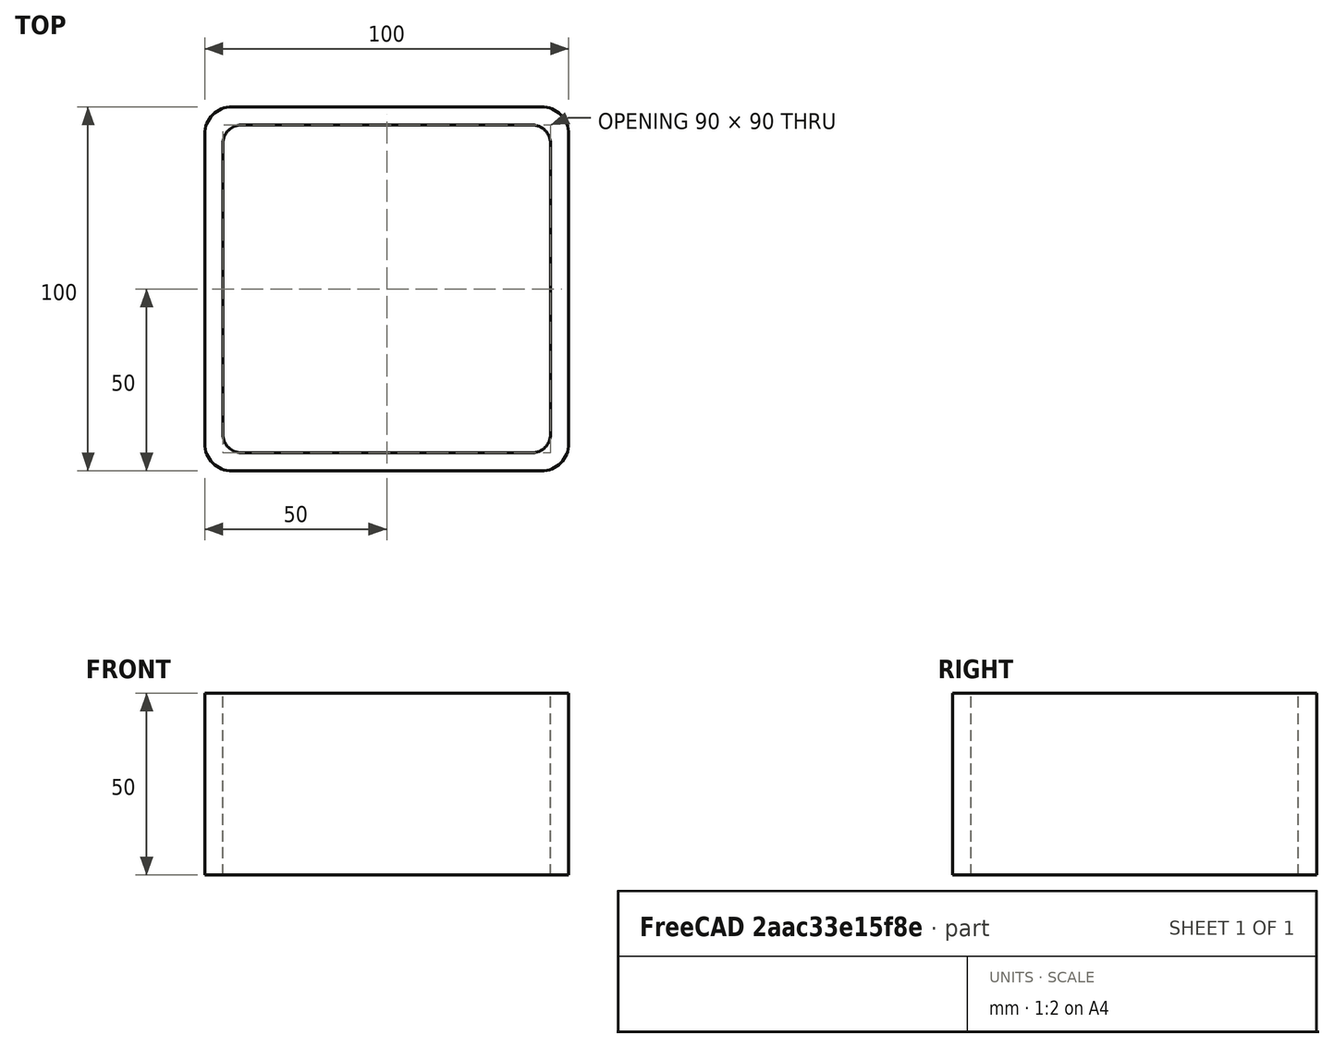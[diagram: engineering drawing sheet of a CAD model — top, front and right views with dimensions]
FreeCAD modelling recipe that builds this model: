
FCSTD DOCUMENT  (FreeCAD 0.15R4671 (Git))
Label: Square hollow section 100x100x5 EN10219 S235JRH
License: All rights reserved
LicenseURL: http://en.wikipedia.org/wiki/All_rights_reserved
objects: Sketcher::SketchObject×1, Part::Extrusion×1
note: 2 computed .brp shape members not serialized (recipe doc carries the construction recipe); baked Part::Feature solids carry a one-line shape summary decoded from their .brp

FEATURE [Sketcher::SketchObject] Sketch
  sketch-geometry (16):
    g0: LineSegment StartX=-40 StartY=45 StartZ=0 EndX=40 EndY=45 EndZ=0
    g1: LineSegment StartX=45 StartY=40 StartZ=0 EndX=45 EndY=-40 EndZ=0
    g2: LineSegment StartX=40 StartY=-45 StartZ=0 EndX=-40 EndY=-45 EndZ=0
    g3: LineSegment StartX=-45 StartY=-40 StartZ=0 EndX=-45 EndY=40 EndZ=0
    g4: LineSegment StartX=-42.5 StartY=50 StartZ=0 EndX=42.5 EndY=50 EndZ=0
    g5: LineSegment StartX=50 StartY=42.5 StartZ=0 EndX=50 EndY=-42.5 EndZ=0
    g6: LineSegment StartX=42.5 StartY=-50 StartZ=0 EndX=-42.5 EndY=-50 EndZ=0
    g7: LineSegment StartX=-50 StartY=-42.5 StartZ=0 EndX=-50 EndY=42.5 EndZ=0
    g8: ArcOfCircle CenterX=-40 CenterY=40 CenterZ=0 NormalX=0 NormalY=0 NormalZ=1 Radius=5 StartAngle=1.5708 EndAngle=3.14159
    g9: ArcOfCircle CenterX=40 CenterY=40 CenterZ=0 NormalX=0 NormalY=0 NormalZ=1 Radius=5 StartAngle=0 EndAngle=1.5708
    g10: ArcOfCircle CenterX=40 CenterY=-40 CenterZ=0 NormalX=0 NormalY=0 NormalZ=1 Radius=5 StartAngle=4.71239 EndAngle=6.28319
    g11: ArcOfCircle CenterX=-40 CenterY=-40 CenterZ=0 NormalX=0 NormalY=0 NormalZ=1 Radius=5 StartAngle=3.14159 EndAngle=4.71239
    g12: ArcOfCircle CenterX=42.5 CenterY=42.5 CenterZ=0 NormalX=0 NormalY=0 NormalZ=1 Radius=7.5 StartAngle=0 EndAngle=1.5708
    g13: ArcOfCircle CenterX=42.5 CenterY=-42.5 CenterZ=0 NormalX=0 NormalY=0 NormalZ=1 Radius=7.5 StartAngle=4.71239 EndAngle=6.28319
    g14: ArcOfCircle CenterX=-42.5 CenterY=-42.5 CenterZ=0 NormalX=0 NormalY=0 NormalZ=1 Radius=7.5 StartAngle=3.14159 EndAngle=4.71239
    g15: ArcOfCircle CenterX=-42.5 CenterY=42.5 CenterZ=0 NormalX=0 NormalY=0 NormalZ=1 Radius=7.5 StartAngle=1.5708 EndAngle=3.14159
  constraints (36):
    c: Horizontal(g2)
    c: Vertical(g3)
    c: Horizontal(g6)
    c: Vertical(g7)
    c: Tangent(g3,g8) = 1.5708
    c: Tangent(g0,g8) = 1.5708
    c: Tangent(g0,g9) = 1.5708
    c: Tangent(g1,g9) = 1.5708
    c: Tangent(g1,g10) = 1.5708
    c: Tangent(g2,g10) = 1.5708
    c: Tangent(g2,g11) = 1.5708
    c: Tangent(g3,g11) = 1.5708
    c: Tangent(g4,g12) = 1.5708
    c: Tangent(g5,g12) = 1.5708
    c: Tangent(g5,g13) = 1.5708
    c: Tangent(g6,g13) = 1.5708
    c: Tangent(g6,g14) = 1.5708
    c: Tangent(g7,g14) = 1.5708
    c: Tangent(g7,g15) = 1.5708
    c: Tangent(g4,g15) = 1.5708
    c: Equal(g9,g8)
    c: Equal(g9,g11)
    c: Equal(g9,g10)
    c: Equal(g12,g15)
    c: Equal(g12,g14)
    c: Equal(g12,g13)
    c: Symmetric(g4,g6,g-1)
    c: Symmetric(g7,g5,g-2)
    c: DistanceY(g4,g6) = -100
    c: DistanceX(g7,g5) = 100
    c: Symmetric(g3,g1,g-2)
    c: Symmetric(g0,g2,g-1)
    c: DistanceY(g0,g4) = 5
    c: DistanceX(g5,g1) = -5
    c: Radius(g9) = 5
    c: Radius(g12) = 7.5
FEATURE [Part::Extrusion] Extrude  label="Square hollow section 100x100x5 EN10219 S235JRH"
  Base = -> Sketch
  Dir = (0,0,50)
  Solid = true
